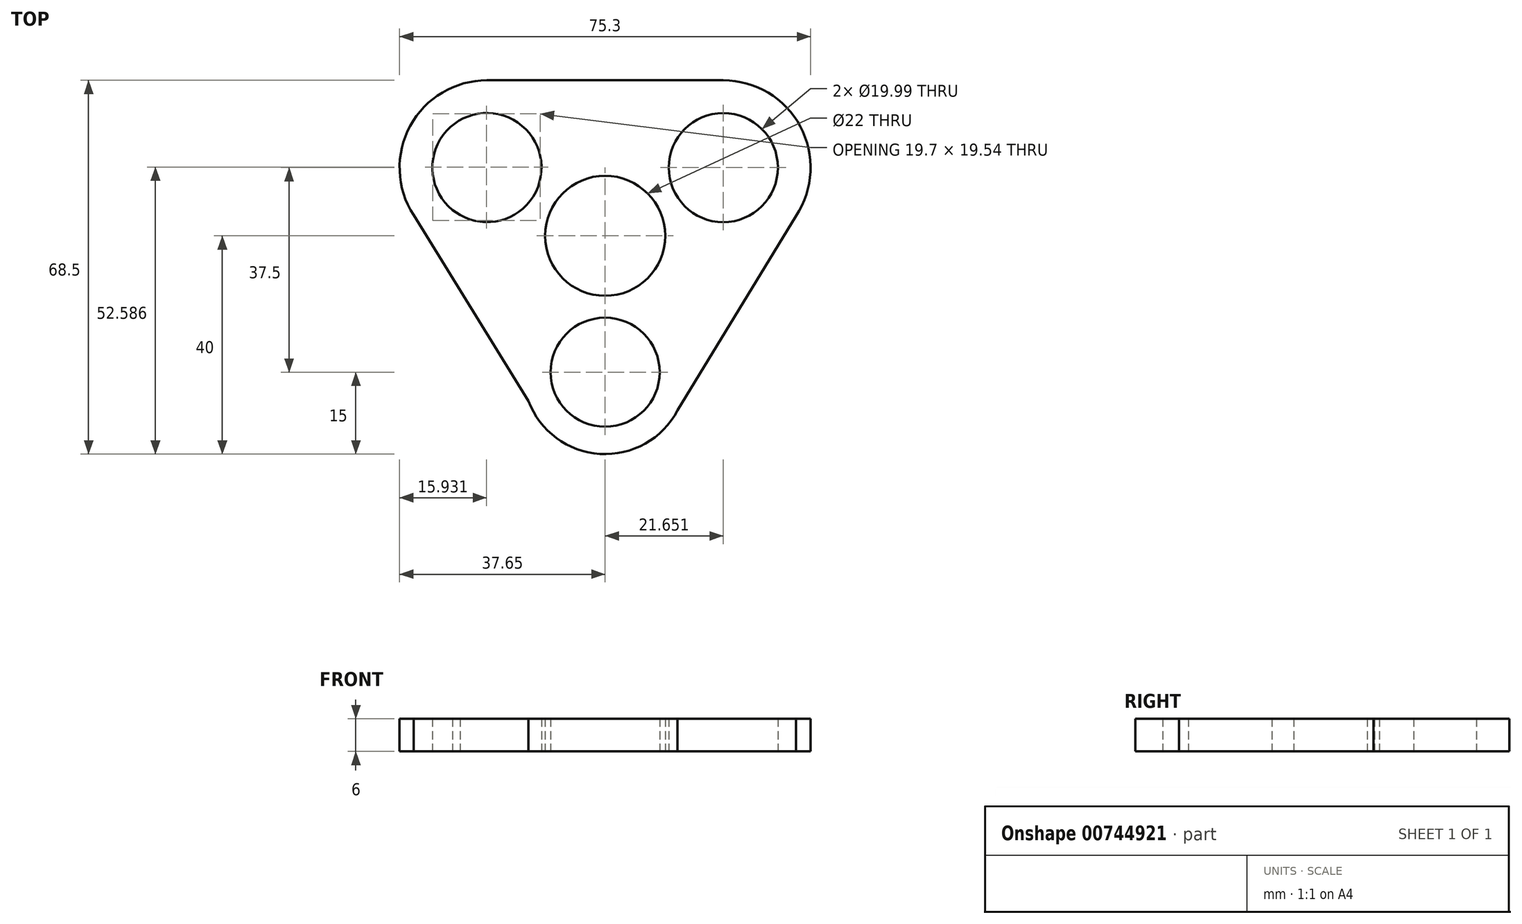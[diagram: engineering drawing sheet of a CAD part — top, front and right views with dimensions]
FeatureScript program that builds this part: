
annotation { "Feature Type Name" : "Feature", "Feature Type Description" : "" }
export const myFeature = defineFeature(function(context is Context, id is Id, definition is map)
    precondition{}
    {
        {
            var Q0;
            Q0=qCreatedBy(makeId("Top.planeOp"),FACE);
            var sketch = newSketch(context, id + "F0", { "sketchPlane" : qUnion([Q0])});
            skCircle(sketch, "E0", {"center": v(0, 0) * mm, "radius": 11 * mm});
            skPoint(sketch, "E1.endSnap0", {"position": v(0, 12.5) * mm});
            skCircle(sketch, "E2", {"center": v(21.65, 12.5) * mm, "radius": 10 * mm});
            skCircle(sketch, "E3", {"center": v(0, -25) * mm, "radius": 10 * mm});
            skArc(sketch, "E4", {"start": v(-26.58, 3.8) * mm, "mid": v(-16.02, 20.76) * mm, "end": v(-27.95, 4.74) * mm});
            skArc(sketch, "E5", {"start": v(-21.65, 28.5) * mm, "mid": v(-35.7, 20.14) * mm, "end": v(-35.08, 3.8) * mm});
            skArc(sketch, "E6", {"start": v(34.97, 3.63) * mm, "mid": v(35.76, 20.05) * mm, "end": v(21.65, 28.5) * mm});
            skArc(sketch, "E7", {"start": v(-14.04, -30.27) * mm, "mid": v(-0.95, -39.97) * mm, "end": v(13.27, -32) * mm});
            skLineSegment(sketch, "E8", {"start": v(-27.95, 4.74) * mm, "end": v(-26.58, 3.8) * mm});
            skPoint(sketch, "E9.end.orphan", {"position": v(-34.38, 22.2) * mm});
            skPoint(sketch, "E10.orphan", {"position": v(34.38, 22.2) * mm});
            skLineSegment(sketch, "E11", {"start": v(21.65, 28.5) * mm, "end": v(-21.65, 28.5) * mm});
            skLineSegment(sketch, "E12", {"start": v(-35.08, 3.8) * mm, "end": v(-11, -35.2) * mm});
            skLineSegment(sketch, "E13", {"start": v(35.64, 4.74) * mm, "end": v(12.3, -33.57) * mm});
            skPoint(sketch, "E14.orphan", {"position": v(14.44, -20.95) * mm});
            skPoint(sketch, "E15.orphan", {"position": v(-14.44, -20.95) * mm});
            skSolve(sketch);
        }
        {
            var Q0;
            Q0 = qSketchRegion(id + "F0", true);
            extrude(context, id + "F1", {"entities" : qUnion([Q0]), "depth" : 6 * mm, "offsetDistance" : 25 * mm});
        }
    });
